# Revit family: Building-IEC309Connections-GEWISS-IEC309HP-10°_FLUSH-MOUNT_SOCKET_16A_IP66-67
name_source: partatom
category: Apparecchi elettrici
units: mm (PartAtom-declared; Revit-internal decimal feet)

## family parameters
Condiviso = Sì
Host = Superficie
Mantenere orientamento annotazione = Sì
Punto di calcolo locali = Sì
Quota connettore circolare = Usa diametro
Taglio con vuoti quando caricato = No
Tipo di parte = Normale

## types (28) — shared parameters
BLOCCO = B=C
Breaking capacity at 1.1 Un = 20A
Catalogue = BUILDING
Corpo centrale = Default(2)
FORMULA = 1000 mm  [stored 3.28084 ft]
Flange dimensions (mm) = 85x75
Glow wire test: = 850 °C (active parts) - 650 °C (passive parts)
IDF = cfe08022-0f95-4975-bb73-0ff941defd52
IDT = 1eeb151f6ea24c4b8ee2ca1def0f5337
IP degree = IP66/IP67
Immagine tipo = <Nessuno>
Insulation resistance = - 10 M?
L = 155 mm  [stored 0.50853 ft]
Operating temperature: = -25 +55 °C
Permissible overload = 22A
Piastra = Default(2)
Produttore = GEWISS S.p.A.
Prospetto di default = 1219 mm
Rated current (A) = 16
SEO = Socket outlet
SPinotto = Default(2)
Shock resistance = IK09
Sportello_visibile = Sì
Spostamento_S = 963 mm
Technical sheet = https://www.gewiss.com
Terminal tightening capacity = 1-2.5mm² flexible cables - 1.5-4mm² rigid cables
Thermo-pressure with ball = 125 °C (active parts) - 80 °C (passive parts)
Total number of operations = -5000
Type of material = Halogen-free in compliance with EN 60754-2
Type of wiring = With screw
Typology = 10° angled flush-mounting socket-outlet
URL = https://www.gewiss.com
Version file RFA = 21.11
W = 115 mm  [stored 0.377297 ft]

## per-type parameters (varying)
| type | Colour: | Descrizione | Electrocod | Frequency | Modello | No. of poles | Rated voltage: | Reference h |
| GW62844H - 10°FL.S.O. HP IP67 3P+E 16A 440÷460V11H | Red | 10°FL.S.O. HP IP67 3P+E 16A 440÷460V11H | 2211 | 60 Hz | GW62844H | 3P+E | 440 - 460 V | 11 |
| GW62226H - 10°FLUSH.S.O. HP IP67 3P+N+E 16A 110V 4H | Yellow | 10°FLUSH.S.O. HP IP67 3P+N+E 16A 110V 4H | 2210 | 50/60 Hz | GW62226H | 3P+N+E | 100 - 130 V | 4 |
| GW62845H - 10°FL.S.O.HP IP67 3P+N+E 16A 440÷460V11H | Red | 10°FL.S.O.HP IP67 3P+N+E 16A 440÷460V11H | 2211 | 60 Hz | GW62845H | 3P+N+E | 440 - 460 V | 11 |
| GW62224H - 10°FLUSH.S.O.  HP IP67 2P+E 16A 110V 4H | Yellow | 10°FLUSH.S.O.  HP IP67 2P+E 16A 110V 4H | 2210 | 50/60 Hz | GW62224H | 2P+E | 100 - 130 V | 4 |
| GW62230H - 10°FLUSH.S.O.  HP IP67 2P+E 16A 400V 9H | Red | 10°FLUSH.S.O.  HP IP67 2P+E 16A 400V 9H | 2210 | 50/60 Hz | GW62230H | 2P+E | 380 - 415 V | 9 |
| GW62839H - 10°FLUSH.S.O.  HP IP67 3P+E 16A-50V 10H | Green | 10°FLUSH.S.O.  HP IP67 3P+E 16A >50V 10H | 2211 | 100 - 300 Hz | GW62839H | 3P+E | -50 V | 10 |
| GW62234H - 10°FLUSH.S.O. HP IP67 3P+N+E 16A 500V 7H | Black | 10°FLUSH.S.O. HP IP67 3P+N+E 16A 500V 7H | 2210 | 50/60 Hz | GW62234H | 3P+N+E | 480 - 500 V | 7 |
| GW62843H - 10°FLUSH.S.O.  HP IP67 3P+N+E 16A-50V2H | Green | 10°FLUSH.S.O.  HP IP67 3P+N+E 16A >50V2H | 2211 | -300 - 500 Hz | GW62843H | 3P+N+E | -50 V | 2 |
| GW62225H - 10°FLUSH.S.O.  HP IP67 3P+E 16A 110V 4H | Yellow | 10°FLUSH.S.O.  HP IP67 3P+E 16A 110V 4H | 2210 | 50/60 Hz | GW62225H | 3P+E | 100 - 130 V | 4 |
| GW62231H - 10°FLUSH.S.O.  HP IP67 3P+E 16A 400V 6H | Red | 10°FLUSH.S.O.  HP IP67 3P+E 16A 400V 6H | 2210 | 50/60 Hz | GW62231H | 3P+E | 380 - 415 V | 6 |
| GW62849H - 10°FLUSH.S.O. HP IP67 3P+E 16A TRASF.12H | Grey | 10°FLUSH.S.O. HP IP67 3P+E 16A TRASF.12H | 2211 | 50/60 Hz | GW62849H | 3P+E | transf. | 12 |
| GW62851H - 10°FLUSH.S.O. HP IP67 2P+E 16A-250Vcc8H | Grey | 10°FLUSH.S.O. HP IP67 2P+E 16A >250Vcc8H | 2211 | d.c. | GW62851H | 2P+E | -250 V | 8 |
| GW62838H - 10°FLUSH.S.O.  HP IP67 2P+E 16A-50V 10H | Green | 10°FLUSH.S.O.  HP IP67 2P+E 16A >50V 10H | 2211 | 100 - 300 Hz | GW62838H | 2P+E | -50 V | 10 |
| GW62227H - 10°FLUSH.S.O.  HP IP67 2P+E 16A 230V 6H | Blue | 10°FLUSH.S.O.  HP IP67 2P+E 16A 230V 6H | 2210 | 50/60 Hz | GW62227H | 2P+E | 200 - 250 V | 6 |
| GW62837H - 10°FLUSH.S.O. HP IP67 3P+N+E 16A 690V 5H | Black | 10°FLUSH.S.O. HP IP67 3P+N+E 16A 690V 5H | 2211 | 50/60 Hz | GW62837H | 3P+N+E | 600 - 690 V | 5 |
| GW62836H - 10°FLUSH.S.O.  HP IP67 3P+E 16A 690V 5H | Black | 10°FLUSH.S.O.  HP IP67 3P+E 16A 690V 5H | 2211 | 50/60 Hz | GW62836H | 3P+E | 600 - 690 V | 5 |
| GW62232H - 10°FLUSH.S.O. HP IP67 3P+N+E 16A 400V 6H | Red | 10°FLUSH.S.O. HP IP67 3P+N+E 16A 400V 6H | 2210 | 50/60 Hz | GW62232H | 3P+N+E | 380 - 415 V | 6 |
| GW62840H - 10°FLUSH.S.O. HP IP67 3P+N+E 16A-50V10H | Green | 10°FLUSH.S.O. HP IP67 3P+N+E 16A >50V10H | 2211 | 100 - 300 Hz | GW62840H | 3P+N+E | -50 V | 10 |
| GW62233H - 10°FLUSH.S.O.  HP IP67 3P+E 16A 500V 7H | Black | 10°FLUSH.S.O.  HP IP67 3P+E 16A 500V 7H | 2210 | 50/60 Hz | GW62233H | 3P+E | 480 - 500 V | 7 |
| GW62842H - 10°FLUSH.S.O.  HP IP67 3P+E 16A-50V 2H | Green | 10°FLUSH.S.O.  HP IP67 3P+E 16A >50V 2H | 2211 | -300 - 500 Hz | GW62842H | 3P+E | -50 V | 2 |
| GW62848H - 10°FLUSH.S.O. HP IP67 2P+E 16A TRASF.12H | Grey | 10°FLUSH.S.O. HP IP67 2P+E 16A TRASF.12H | 2211 | 50/60 Hz | GW62848H | 2P+E | transf. | 12 |
| GW62850H - 10°FL.S.O. HP IP67 2P+E 16A-50÷250Vcc3H | Grey | 10°FL.S.O. HP IP67 2P+E 16A >50÷250Vcc3H | 2211 | d.c. | GW62850H | 2P+E | -50 - 250 V | 3 |
| GW62847H - 10°FL.S.O. HP IP67 3P+N+E 16A 380/440V3H | Red | 10°FL.S.O. HP IP67 3P+N+E 16A 380/440V3H | 2211 | 50/60 Hz | GW62847H | 3P+N+E | 380 - 440 V | 3 |
| GW62846H - 10°FLUSH.S.O.HP IP67 3P+E 16A 380/440V3H | Red | 10°FLUSH.S.O.HP IP67 3P+E 16A 380/440V3H | 2211 | 50/60 Hz | GW62846H | 3P+E | 380 - 440 V | 3 |
| GW62229H - 10°FLUSH.S.O. HP IP67 3P+N+E 16A 230V 9H | Blue | 10°FLUSH.S.O. HP IP67 3P+N+E 16A 230V 9H | 2210 | 50/60 Hz | GW62229H | 3P+N+E | 200 - 250 V | 9 |
| GW62835H - 10°FLUSH.S.O.  HP IP67 2P+E 16A 500V 7H | Black | 10°FLUSH.S.O.  HP IP67 2P+E 16A 500V 7H | 2211 | 50/60 Hz | GW62835H | 2P+E | 480 - 500 V | 7 |
| GW62841H - 10°FLUSH.S.O.  HP IP67 2P+E 16A-50V 2H | Green | 10°FLUSH.S.O.  HP IP67 2P+E 16A >50V 2H | 2211 | -300 - 500 Hz | GW62841H | 2P+E | -50 V | 2 |
| GW62228H - 10°FLUSH.S.O.  HP IP67 3P+E 16A 230V 9H | Blue | 10°FLUSH.S.O.  HP IP67 3P+E 16A 230V 9H | 2210 | 50/60 Hz | GW62228H | 3P+E | 200 - 250 V | 9 |

note: [stored X ft] marks values corroborated as IEEE doubles in the binary element streams (Revit-internal decimal feet)

## geometry (parser evidence)
native form markers: Sweep x1
no freeform markers — native parametric forms only
